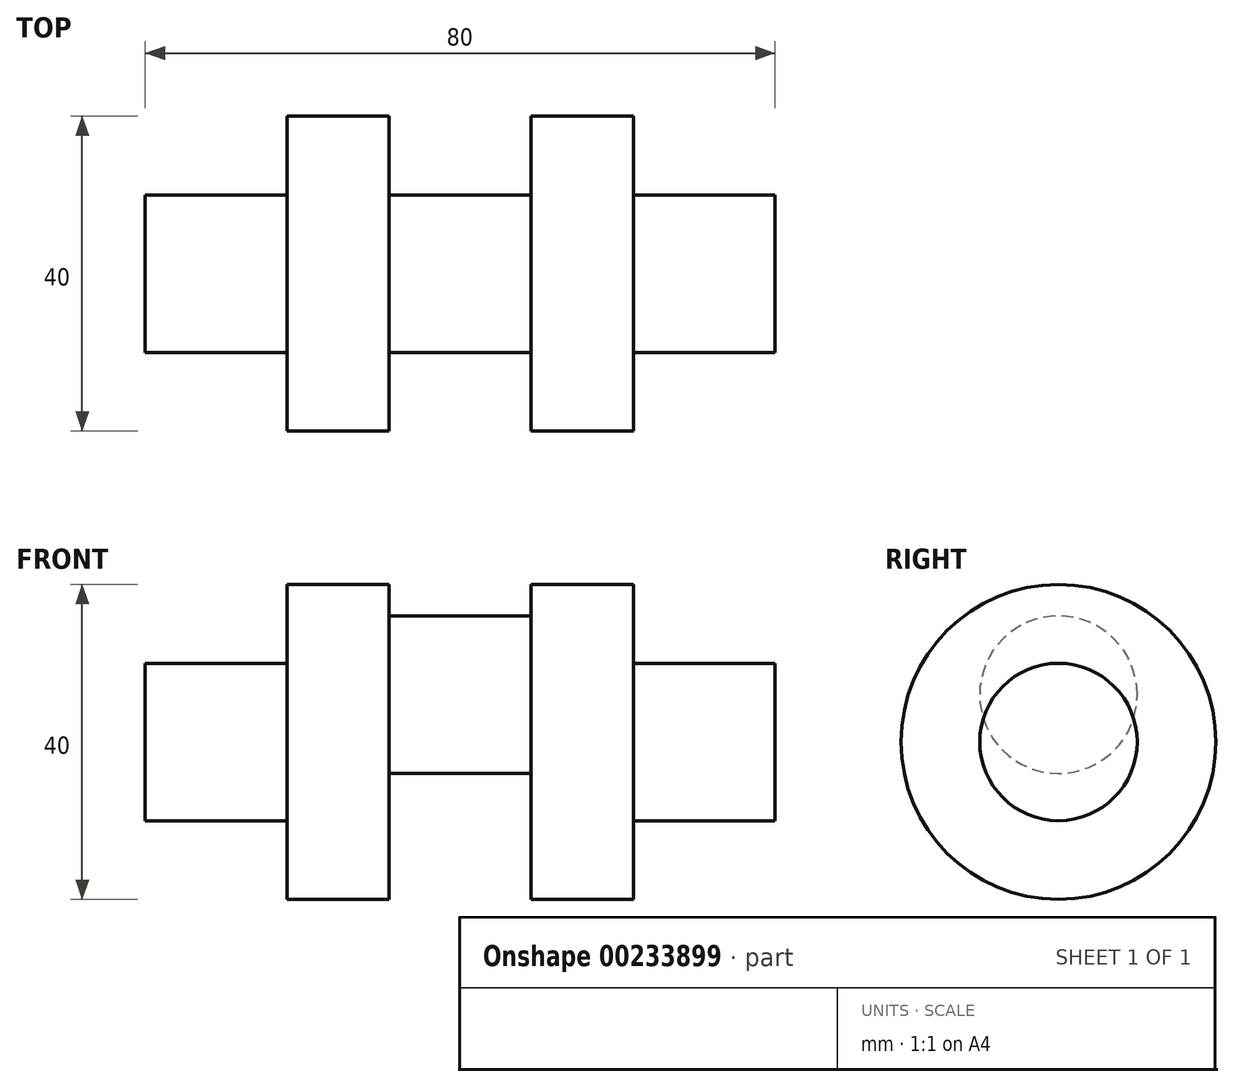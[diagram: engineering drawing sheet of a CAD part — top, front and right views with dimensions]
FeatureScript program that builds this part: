
annotation { "Feature Type Name" : "Feature", "Feature Type Description" : "" }
export const myFeature = defineFeature(function(context is Context, id is Id, definition is map)
    precondition{}
    {
        {
            var Q0;
            Q0=qCreatedBy(makeId("Front.planeOp"),FACE);
            var sketch = newSketch(context, id + "F0", { "sketchPlane" : qUnion([Q0])});
            skLineSegment(sketch, "E0", {"start": v(-71.32, 0) * mm, "end": v(70, 0) * mm});
            skLineSegment(sketch, "E1", {"start": v(-55.47, 0) * mm, "end": v(-55.47, 10) * mm});
            skLineSegment(sketch, "E2", {"start": v(-55.47, 10) * mm, "end": v(-37.47, 10) * mm});
            skLineSegment(sketch, "E3", {"start": v(-37.47, 10) * mm, "end": v(-37.47, 0) * mm});
            skLineSegment(sketch, "E4", {"start": v(-37.47, 10) * mm, "end": v(-37.47, 20) * mm});
            skLineSegment(sketch, "E5", {"start": v(-37.47, 20) * mm, "end": v(-24.47, 20) * mm});
            skLineSegment(sketch, "E6", {"start": v(-24.47, 20) * mm, "end": v(-24.47, 0) * mm});
            skLineSegment(sketch, "E7", {"start": v(-24.47, 16) * mm, "end": v(-6.47, 16) * mm});
            skLineSegment(sketch, "E8", {"start": v(-6.47, 16) * mm, "end": v(-6.47, 6) * mm});
            skLineSegment(sketch, "E9", {"start": v(-6.47, 6) * mm, "end": v(-24.47, 6) * mm});
            skLineSegment(sketch, "E10", {"start": v(-6.47, 16) * mm, "end": v(-6.47, 20) * mm});
            skLineSegment(sketch, "E11", {"start": v(-6.47, 20) * mm, "end": v(6.53, 20) * mm});
            skLineSegment(sketch, "E12", {"start": v(6.53, 20) * mm, "end": v(6.53, 0) * mm});
            skLineSegment(sketch, "E13", {"start": v(-6.47, 6) * mm, "end": v(-6.47, 0) * mm});
            skLineSegment(sketch, "E14", {"start": v(6.53, 10) * mm, "end": v(24.53, 10) * mm});
            skLineSegment(sketch, "E15", {"start": v(24.53, 10) * mm, "end": v(24.53, 0) * mm});
            skLineSegment(sketch, "E16", {"start": v(-37.47, 0) * mm, "end": v(-24.47, 0) * mm});
            skLineSegment(sketch, "E17", {"start": v(-24.47, 0) * mm, "end": v(-6.47, 0) * mm});
            skLineSegment(sketch, "E18", {"start": v(-6.47, 0) * mm, "end": v(6.53, 0) * mm});
            skLineSegment(sketch, "E19", {"start": v(6.53, 0) * mm, "end": v(24.53, 0) * mm});
            skLineSegment(sketch, "E20", {"start": v(-24.47, 11) * mm, "end": v(-6.47, 11) * mm, "construction": true});
            skSolve(sketch);
        }
        {
            var Q0;
            {var subQ0=sQuery(id+"F0.wireOp",EDGE,"E1");Q0=makeQuery(id+"F0.imprint","IMPRINT",FACE,{"disambiguationData":[TD([[makeQuery(id+"F0.imprint","IMPRINT",EDGE,{"derivedFrom":subQ0}),-1.0]])]});}
            var Q1;
            Q1=makeQuery(id+"F0.imprint","IMPRINT",FACE,{"disambiguationData":[TD([[makeQuery(id+"F0.imprint","IMPRINT",EDGE,{"derivedFrom":sQuery(id+"F0.wireOp",EDGE,"E3")}),1.0]])]});
            var Q2;
            Q2=makeQuery(id+"F0.imprint","IMPRINT",FACE,{"disambiguationData":[TD([[makeQuery(id+"F0.imprint","IMPRINT",EDGE,{"derivedFrom":sQuery(id+"F0.wireOp",EDGE,"E8")}),1.0]])]});
            var Q3;
            {var subQ2=sQuery(id+"F0.wireOp",EDGE,"E14");Q3=makeQuery(id+"F0.imprint","IMPRINT",FACE,{"disambiguationData":[TD([[makeQuery(id+"F0.imprint","IMPRINT",EDGE,{"derivedFrom":subQ2}),-1.0]])]});}
            var Q4;
            Q4=sQuery(id+"F0.wireOp",EDGE,"E0");
            revolve(context, id + "F1", {"entities" : qUnion([Q0, Q1, Q2, Q3]), "axis" : qUnion([Q4]), "revolveType" : RevolveType.FULL});
        }
        {
            var Q0;
            {var subQ0=sQuery(id+"F0.wireOp",EDGE,"E7");Q0=makeQuery(id+"F0.imprint","IMPRINT",FACE,{"disambiguationData":[TD([[makeQuery(id+"F0.imprint","IMPRINT",EDGE,{"derivedFrom":subQ0}),-1.0]])]});}
            var Q1;
            Q1=sQuery(id+"F0.wireOp",EDGE,"E9");
            revolve(context, id + "F2", {"operationType" : NewBodyOperationType.ADD, "entities" : qUnion([Q0]), "axis" : qUnion([Q1]), "revolveType" : RevolveType.FULL});
        }
    });
